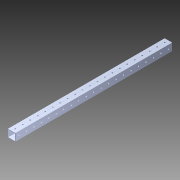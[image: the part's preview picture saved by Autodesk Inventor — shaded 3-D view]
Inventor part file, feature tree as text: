
AUTODESK INVENTOR PART (.ipt)
format: ipt  version: 2014 SP1 (Build 180222100, 222)  size: 1,201,664 bytes
history: native  units: in
note: dims shown in document units (in); Inventor stores cm internally (conversion verified against a paired STEP export)
features: pattern_circular x1, other x1, extrude x1, imported_body x1, sketch x1
ambient origin geometry x8: Origin, YZ Plane, XZ Plane, XY Plane, X Axis, Y Axis, Z Axis, Center Point
bodies: Body1 (feature_tree)
feature tree (5):
  pattern_circular  "CirPattern2"
  other  "1x1 tube1"
  extrude  "Extrusion1"  [1 undecoded]
  imported_body  "Base1"
  sketch  "Sketch1"  dims[d0=38.0in d1=0.0in]
note: 1 required parameter value undecoded (feature->parameter linkage not recoverable at this tier; creation-order binding heuristic only, values carry confidence <= 0.55)
